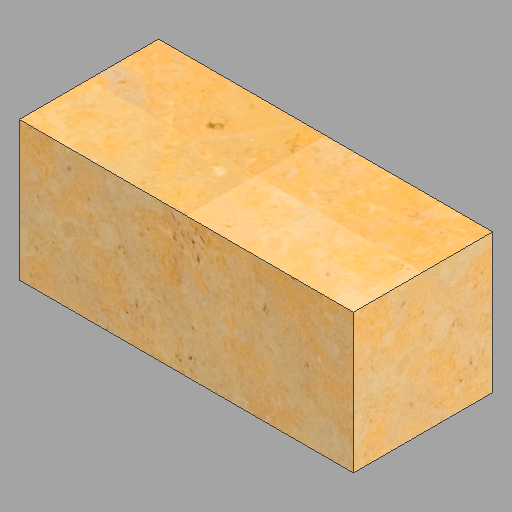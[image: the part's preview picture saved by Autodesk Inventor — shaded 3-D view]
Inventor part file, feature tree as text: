
AUTODESK INVENTOR PART (.ipt)
format: ipt  version: 2023 (Build 270158030, 158C)  size: 379,392 bytes
history: native  units: in
note: dims shown in document units (in); Inventor stores cm internally (conversion verified against a paired STEP export)
features: extrude x1, sketch x1
ambient origin geometry x8: Origin, YZ Plane, XZ Plane, XY Plane, X Axis, Y Axis, Z Axis, Center Point
bodies: Solid1 (feature_tree)
feature tree (2):
  extrude  "Extrusion1"  Depth=5.0in
  sketch  "Sketch1"  dims[d0=12.0in d1=5.0in d2=5.0in d3=0.0in]
